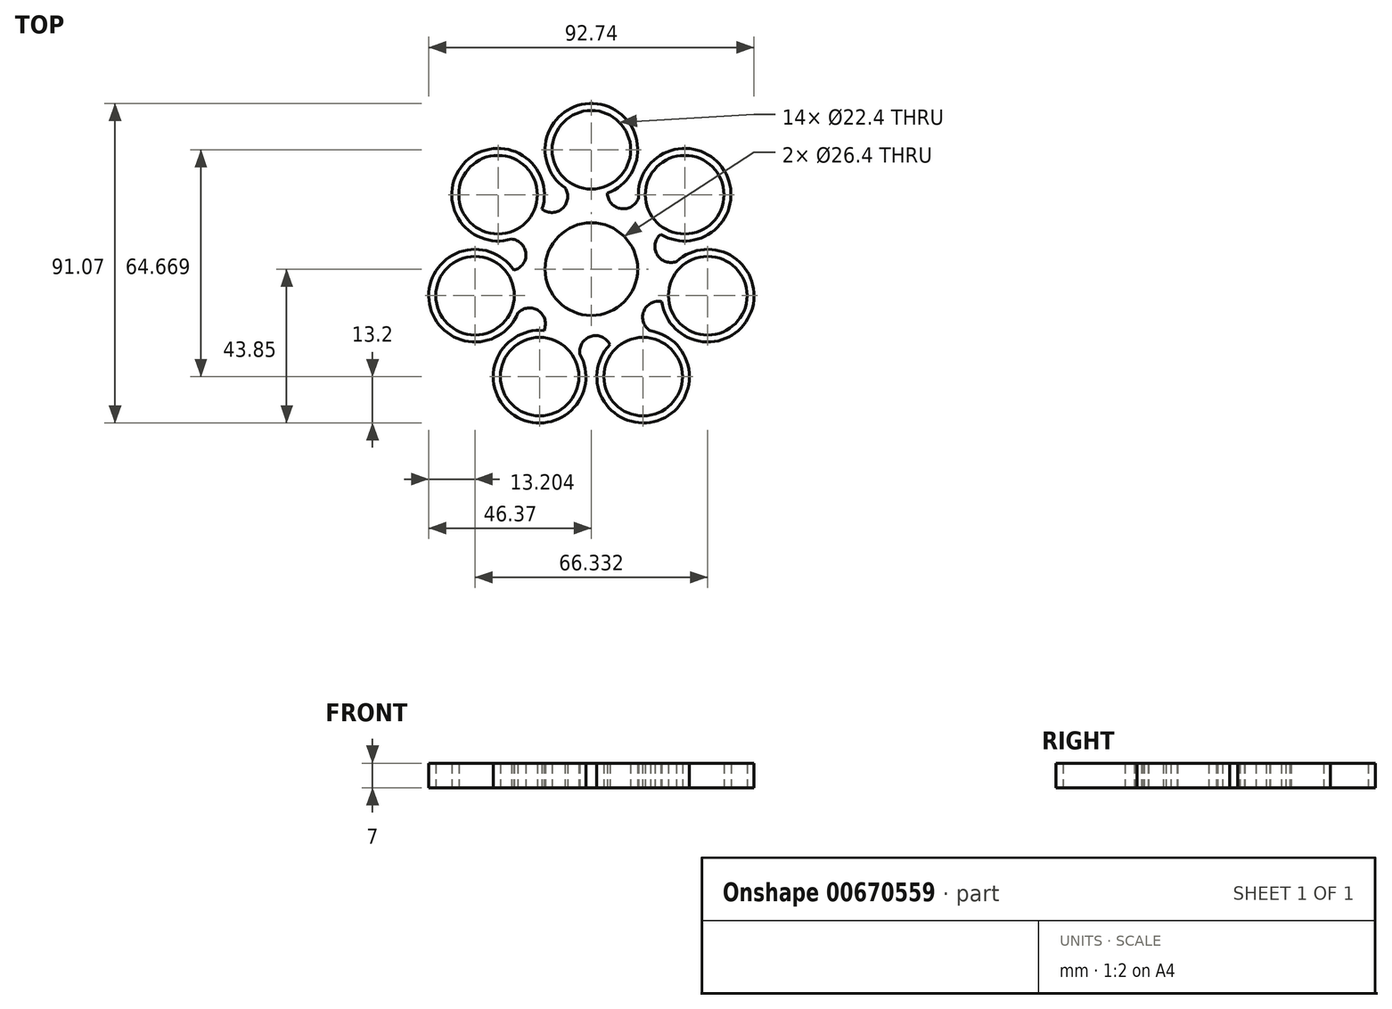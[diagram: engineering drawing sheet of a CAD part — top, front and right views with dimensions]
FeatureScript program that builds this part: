
annotation { "Feature Type Name" : "Feature", "Feature Type Description" : "" }
export const myFeature = defineFeature(function(context is Context, id is Id, definition is map)
    precondition{}
    {
        {
            var Q0;
            Q0=qCreatedBy(makeId("Top.planeOp"),FACE);
            var sketch = newSketch(context, id + "F0", { "sketchPlane" : qUnion([Q0])});
            skCircle(sketch, "E0", {"center": v(0, 0) * mm, "radius": 11.2 * mm});
            skCircle(sketch, "E1", {"center": v(0, 0) * mm, "radius": 13.2 * mm});
            skCircle(sketch, "E2", {"center": v(0, 34.02) * mm, "radius": 11.2 * mm});
            skCircle(sketch, "E3", {"center": v(0, 34.02) * mm, "radius": 13.2 * mm});
            skCircle(sketch, "E4.1.0", {"center": v(-26.6, 21.21) * mm, "radius": 13.2 * mm});
            skCircle(sketch, "E4.1.1", {"center": v(-26.6, 21.21) * mm, "radius": 11.2 * mm});
            skCircle(sketch, "E4.2.0", {"center": v(-33.17, -7.57) * mm, "radius": 13.2 * mm});
            skCircle(sketch, "E4.2.1", {"center": v(-33.17, -7.57) * mm, "radius": 11.2 * mm});
            skCircle(sketch, "E4.3.0", {"center": v(-14.76, -30.65) * mm, "radius": 13.2 * mm});
            skCircle(sketch, "E4.3.1", {"center": v(-14.76, -30.65) * mm, "radius": 11.2 * mm});
            skCircle(sketch, "E4.4.0", {"center": v(14.76, -30.65) * mm, "radius": 13.2 * mm});
            skCircle(sketch, "E4.4.1", {"center": v(14.76, -30.65) * mm, "radius": 11.2 * mm});
            skCircle(sketch, "E4.5.0", {"center": v(33.17, -7.57) * mm, "radius": 13.2 * mm});
            skCircle(sketch, "E4.5.1", {"center": v(33.17, -7.57) * mm, "radius": 11.2 * mm});
            skCircle(sketch, "E4.6.0", {"center": v(26.6, 21.21) * mm, "radius": 13.2 * mm});
            skCircle(sketch, "E4.6.1", {"center": v(26.6, 21.21) * mm, "radius": 11.2 * mm});
            skArc(sketch, "E5", {"start": v(-14.06, 17.08) * mm, "mid": v(-8.2, 17.34) * mm, "end": v(-7.53, 23.18) * mm});
            skArc(sketch, "E6.1.0", {"start": v(-22.12, -0.34) * mm, "mid": v(-18.67, 4.4) * mm, "end": v(-22.82, 8.56) * mm});
            skArc(sketch, "E6.2.0", {"start": v(-13.53, -17.5) * mm, "mid": v(-15.09, -11.85) * mm, "end": v(-20.92, -12.5) * mm});
            skArc(sketch, "E6.3.0", {"start": v(5.25, -21.5) * mm, "mid": v(-0.14, -19.18) * mm, "end": v(-3.27, -24.15) * mm});
            skArc(sketch, "E6.4.0", {"start": v(20.08, -9.3) * mm, "mid": v(14.9, -12.07) * mm, "end": v(16.84, -17.62) * mm});
            skArc(sketch, "E6.5.0", {"start": v(19.78, 9.9) * mm, "mid": v(18.73, 4.13) * mm, "end": v(24.27, 2.19) * mm});
            skArc(sketch, "E6.6.0", {"start": v(4.6, 21.64) * mm, "mid": v(8.45, 17.22) * mm, "end": v(13.43, 20.34) * mm});
            skSolve(sketch);
        }
        {
            var Q0;
            Q0=makeQuery(id+"F0.imprint","IMPRINT",FACE,{"disambiguationData":[TD([[makeQuery(id+"F0.imprint","IMPRINT",EDGE,{"derivedFrom":sQuery(id+"F0.wireOp",EDGE,"E4.6.1")}),-1.0]])]});
            var Q1;
            Q1=makeQuery(id+"F0.imprint","IMPRINT",FACE,{"disambiguationData":[TD([[makeQuery(id+"F0.imprint","IMPRINT",EDGE,{"derivedFrom":sQuery(id+"F0.wireOp",EDGE,"E1")}),-1.0]])]});
            var Q2;
            Q2=makeQuery(id+"F0.imprint","IMPRINT",FACE,{"disambiguationData":[TD([[makeQuery(id+"F0.imprint","IMPRINT",EDGE,{"derivedFrom":sQuery(id+"F0.wireOp",EDGE,"E4.4.1")}),-1.0]])]});
            var Q3;
            Q3=makeQuery(id+"F0.imprint","IMPRINT",FACE,{"disambiguationData":[TD([[makeQuery(id+"F0.imprint","IMPRINT",EDGE,{"derivedFrom":sQuery(id+"F0.wireOp",EDGE,"E4.3.1")}),-1.0]])]});
            var Q4;
            Q4=makeQuery(id+"F0.imprint","IMPRINT",FACE,{"disambiguationData":[TD([[makeQuery(id+"F0.imprint","IMPRINT",EDGE,{"derivedFrom":sQuery(id+"F0.wireOp",EDGE,"E4.5.1")}),-1.0]])]});
            var Q5;
            Q5=makeQuery(id+"F0.imprint","IMPRINT",FACE,{"disambiguationData":[TD([[makeQuery(id+"F0.imprint","IMPRINT",EDGE,{"derivedFrom":sQuery(id+"F0.wireOp",EDGE,"E2")}),-1.0]])]});
            var Q6;
            Q6=makeQuery(id+"F0.imprint","IMPRINT",FACE,{"disambiguationData":[TD([[makeQuery(id+"F0.imprint","IMPRINT",EDGE,{"derivedFrom":sQuery(id+"F0.wireOp",EDGE,"E4.1.1")}),-1.0]])]});
            var Q7;
            Q7=makeQuery(id+"F0.imprint","IMPRINT",FACE,{"disambiguationData":[TD([[makeQuery(id+"F0.imprint","IMPRINT",EDGE,{"derivedFrom":sQuery(id+"F0.wireOp",EDGE,"E4.2.1")}),-1.0]])]});
            extrude(context, id + "F1", {"entities" : qUnion([Q0, Q1, Q2, Q3, Q4, Q5, Q6, Q7]), "depth" : 7 * mm, "offsetDistance" : 25 * mm});
        }
    });
